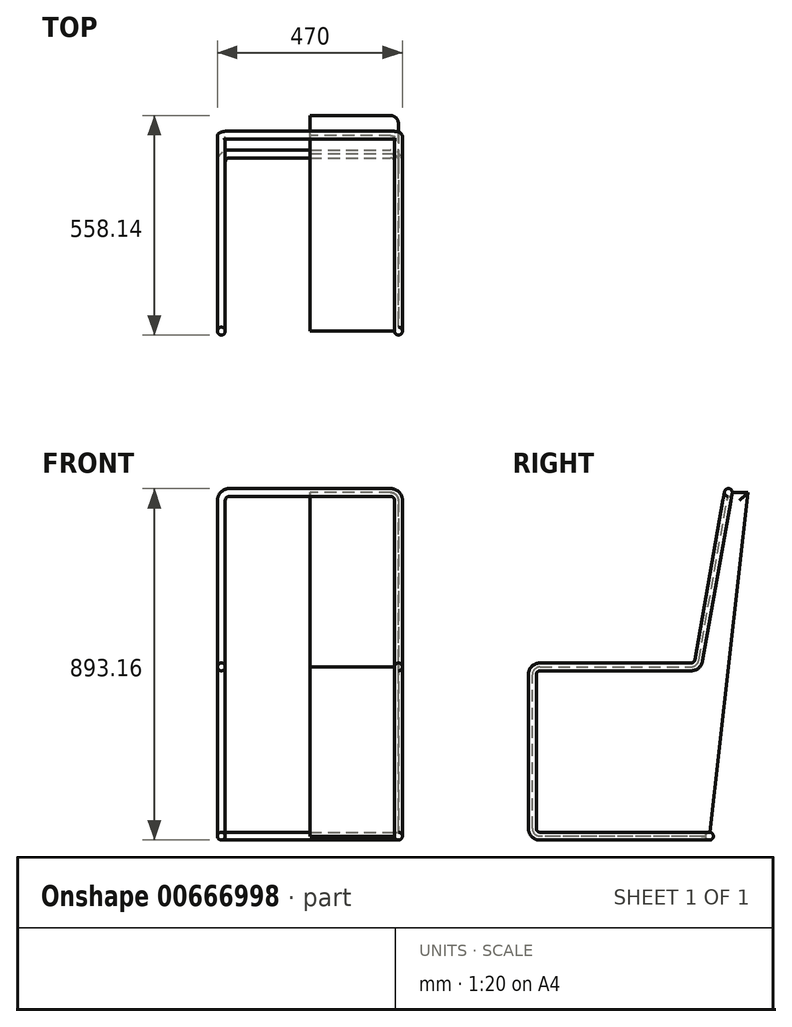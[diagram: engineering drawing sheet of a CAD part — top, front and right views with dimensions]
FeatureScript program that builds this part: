
annotation { "Feature Type Name" : "Feature", "Feature Type Description" : "" }
export const myFeature = defineFeature(function(context is Context, id is Id, definition is map)
    precondition{}
    {
        {
            var Q0;
            Q0=qCreatedBy(makeId("Right.planeOp"),FACE);
            var sketch = newSketch(context, id + "F0", { "sketchPlane" : qUnion([Q0])});
            skLineSegment(sketch, "E0", {"start": v(0, 0) * mm, "end": v(-450, 0) * mm});
            skLineSegment(sketch, "E1", {"start": v(-450, 0) * mm, "end": v(-450, 430) * mm});
            skLineSegment(sketch, "E2", {"start": v(-450, 430) * mm, "end": v(-30, 430) * mm});
            skLineSegment(sketch, "E3", {"start": v(-30, 430) * mm, "end": v(48.14, 873.16) * mm});
            skLineSegment(sketch, "E4", {"start": v(48.14, 873.16) * mm, "end": v(98.14, 873.16) * mm});
            skLineSegment(sketch, "E5", {"start": v(98.14, 873.16) * mm, "end": v(0, 0) * mm});
            skSolve(sketch);
        }
        {
            var Q0;
            Q0 = qSketchRegion(id + "F0", true);
            extrude(context, id + "F1", {"entities" : qUnion([Q0]), "depth" : 225 * mm, "offsetDistance" : 25 * mm});
        }
        {
            var Q0;
            Q0=makeQuery(id+"F1.opExtrude","CAP_EDGE",EDGE,{"disambiguationData":[OSD([sQuery(id+"F0.wireOp",EDGE,"E5")])],"isStart":false});
            var Q1;
            Q1=makeQuery(id+"F1.opExtrude","SWEPT_EDGE",EDGE,{"disambiguationData":[OSD([sQuery(id+"F0.wireOp",EDGE,"E2"),sQuery(id+"F0.wireOp",EDGE,"E3")])]});
            var Q2;
            Q2=makeQuery(id+"F1.opExtrude","CAP_EDGE",EDGE,{"disambiguationData":[OSD([sQuery(id+"F0.wireOp",EDGE,"E4")])],"isStart":false});
            var Q3;
            Q3=makeQuery(id+"F1.opExtrude","SWEPT_EDGE",EDGE,{"disambiguationData":[OSD([sQuery(id+"F0.wireOp",EDGE,"E1"),sQuery(id+"F0.wireOp",EDGE,"E2")])]});
            var Q4;
            Q4=makeQuery(id+"F1.opExtrude","SWEPT_EDGE",EDGE,{"disambiguationData":[OSD([sQuery(id+"F0.wireOp",EDGE,"E0"),sQuery(id+"F0.wireOp",EDGE,"E1")])]});
            fillet(context, id + "F2", {"entities" : qUnion([Q0, Q1, Q2, Q3, Q4]), "radius" : 20 * mm, "tangentPropagation" : true, "allowEdgeOverflow" : false});
        }
        {
            var Q0;
            Q0=makeQuery(id+"F1.opExtrude","CAP_FACE",FACE,{"disambiguationData":[OSD([sQuery(id+"F0.wireOp",EDGE,"E0"),sQuery(id+"F0.wireOp",EDGE,"E1"),sQuery(id+"F0.wireOp",EDGE,"E2"),sQuery(id+"F0.wireOp",EDGE,"E3"),sQuery(id+"F0.wireOp",EDGE,"E4"),sQuery(id+"F0.wireOp",EDGE,"E5")])],"isStart":false});
            var sketch = newSketch(context, id + "F3", { "sketchPlane" : qUnion([Q0])});
            skArc(sketch, "E6.0", {"start": v(-430, 430) * mm, "mid": v(-444.14, 424.14) * mm, "end": v(-450, 410) * mm});
            skLineSegment(sketch, "E6.1", {"start": v(-430, 430) * mm, "end": v(-46.78, 430) * mm});
            skLineSegment(sketch, "E6.2", {"start": v(-450, 20) * mm, "end": v(-450, 410) * mm});
            skArc(sketch, "E6.3", {"start": v(-27.09, 446.53) * mm, "mid": v(-33.93, 434.68) * mm, "end": v(-46.78, 430) * mm});
            skLineSegment(sketch, "E6.4", {"start": v(-27.09, 446.53) * mm, "end": v(44.62, 853.16) * mm});
            skLineSegment(sketch, "E6.5", {"start": v(-20.13, 0) * mm, "end": v(-430, 0) * mm});
            skArc(sketch, "E6.6", {"start": v(-450, 20) * mm, "mid": v(-444.14, 5.86) * mm, "end": v(-430, 0) * mm});
            skSolve(sketch);
        }
        {
            var Q0;
            Q0=makeQuery(id+"F1.opExtrude","SWEPT_FACE",FACE,{"disambiguationData":[OSD([sQuery(id+"F0.wireOp",EDGE,"E3")])]});
            var sketch = newSketch(context, id + "F4", { "sketchPlane" : qUnion([Q0])});
            skEllipticalArc(sketch, "E7.0", {});
            skLineSegment(sketch, "E7.1", {"start": v(205, 868.26) * mm, "end": v(0, 868.26) * mm});
            const initialGuessF4  = {"E7.0": [0.205, 0.8479493562275267, 0, 1, 0.020308532237714897, 0.02, 4.71238898038469, 0]};
            skSetInitialGuess(sketch, initialGuessF4);
            skSolve(sketch);
        }
        {
            var Q0;
            Q0=makeQuery(id+"F1.opExtrude","SWEPT_FACE",FACE,{"disambiguationData":[OSD([sQuery(id+"F0.wireOp",EDGE,"E0")])]});
            var sketch = newSketch(context, id + "F5", { "sketchPlane" : qUnion([Q0])});
            skLineSegment(sketch, "E8.0", {"start": v(205, 0) * mm, "end": v(0, 0) * mm});
            skEllipticalArc(sketch, "E8.1", {});
            const initialGuessF5  = {"E8.1": [0.205, 0.020125936219912054, 0, 1, 0.02012593621991206, 0.02, 3.141592653589793, 4.71238898038469]};
            skSetInitialGuess(sketch, initialGuessF5);
            skSolve(sketch);
        }
        {
            var Q0;
            Q0=qCreatedBy(makeId("Right.planeOp"),FACE);
            var sketch = newSketch(context, id + "F6", { "sketchPlane" : qUnion([Q0])});
            skCircle(sketch, "E9", {"center": v(0, 0) * mm, "radius": 10 * mm});
            skSolve(sketch);
        }
        {
            var Q0;
            Q0=makeQuery(id+"F6.imprint","IMPRINT",FACE,{"disambiguationData":[TD([[makeQuery(id+"F6.imprint","IMPRINT",EDGE,{"derivedFrom":sQuery(id+"F6.wireOp",EDGE,"E9")}),1.0]])]});
            var Q1;
            Q1=sQuery(id+"F5.wireOp",EDGE,"E8.0");
            var Q2;
            Q2=sQuery(id+"F5.wireOp",EDGE,"E8.1");
            var Q3;
            Q3=sQuery(id+"F3.wireOp",EDGE,"E6.5");
            var Q4;
            Q4=sQuery(id+"F3.wireOp",EDGE,"E6.6");
            var Q5;
            Q5=sQuery(id+"F3.wireOp",EDGE,"E6.2");
            var Q6;
            Q6=sQuery(id+"F3.wireOp",EDGE,"E6.0");
            var Q7;
            Q7=sQuery(id+"F3.wireOp",EDGE,"E6.1");
            var Q8;
            Q8=sQuery(id+"F3.wireOp",EDGE,"E6.3");
            var Q9;
            Q9=sQuery(id+"F3.wireOp",EDGE,"E6.4");
            var Q10;
            Q10=sQuery(id+"F4.wireOp",EDGE,"E7.0");
            var Q11;
            Q11=sQuery(id+"F4.wireOp",EDGE,"E7.1");
            sweep(context, id + "F7", {"profiles" : qUnion([Q0]), "path" : qUnion([Q1, Q2, Q3, Q4, Q5, Q6, Q7, Q8, Q9, Q10, Q11])});
        }
        {
            var Q0;
            Q0=makeQuery(id+"F7.opSweep","SWEPT_BODY",BODY,{"disambiguationData":[OSD([sQuery(id+"F4.wireOp",EDGE,"E7.1"),sQuery(id+"F6.wireOp",EDGE,"E9")])]});
            var Q1;
            Q1=qCreatedBy(makeId("Right.planeOp"),FACE);
            mirror(context, id + "F8", {"operationType" : NewBodyOperationType.ADD, "entities" : qUnion([Q0]), "mirrorPlane" : qUnion([Q1])});
        }
    });
